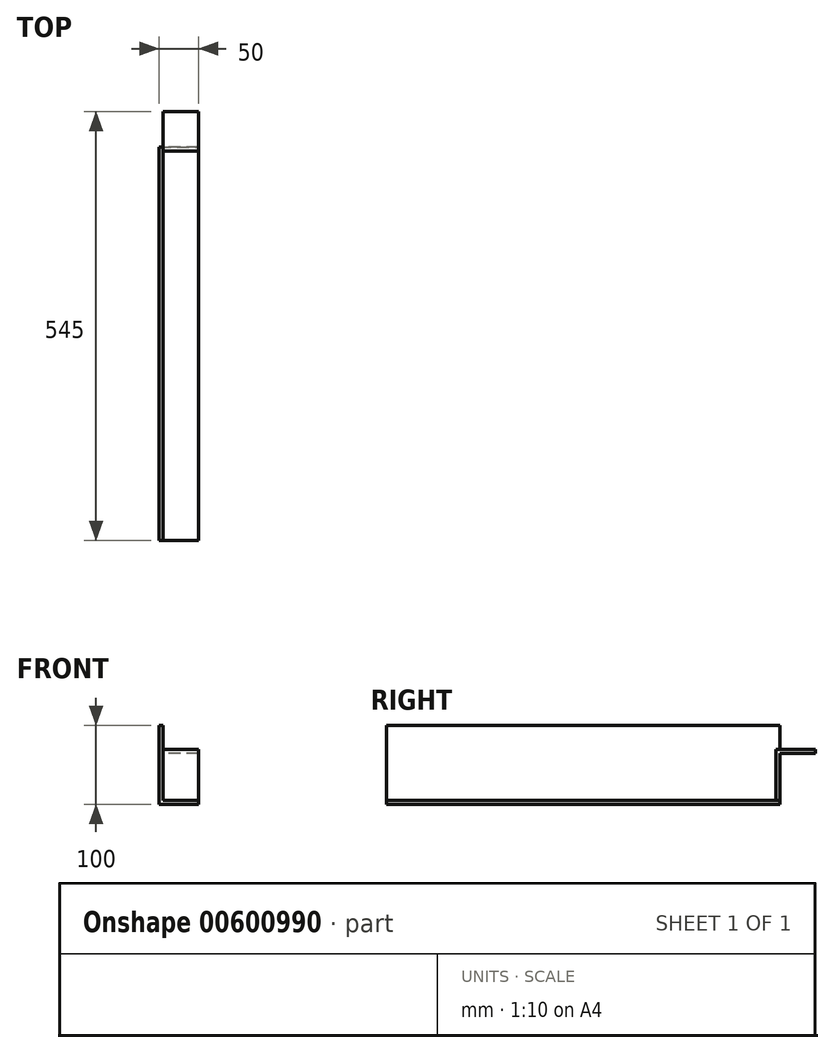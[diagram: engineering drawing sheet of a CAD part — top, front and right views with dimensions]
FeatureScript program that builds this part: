
annotation { "Feature Type Name" : "Feature", "Feature Type Description" : "" }
export const myFeature = defineFeature(function(context is Context, id is Id, definition is map)
    precondition{}
    {
        {
            var Q0;
            Q0=qCreatedBy(makeId("Front.planeOp"),FACE);
            var sketch = newSketch(context, id + "F0", { "sketchPlane" : qUnion([Q0])});
            skLineSegment(sketch, "E0.bottom", {"start": v(0, 0) * mm, "end": v(50, 0) * mm});
            skLineSegment(sketch, "E0.top", {"start": v(0, 100) * mm, "end": v(5, 100) * mm});
            skLineSegment(sketch, "E0.left", {"start": v(0, 0) * mm, "end": v(0, 100) * mm});
            skLineSegment(sketch, "E0.right", {"start": v(50, 0) * mm, "end": v(50, 5) * mm});
            skLineSegment(sketch, "E1.0", {"start": v(5, 5) * mm, "end": v(5, 100) * mm});
            skLineSegment(sketch, "E2.0", {"start": v(5, 5) * mm, "end": v(50, 5) * mm});
            skSolve(sketch);
        }
        {
            var Q0;
            Q0=makeQuery(id+"F0.imprint","IMPRINT",FACE,{"disambiguationData":[TD([[makeQuery(id+"F0.imprint","IMPRINT",EDGE,{"derivedFrom":sQuery(id+"F0.wireOp",EDGE,"E0.bottom")}),1.0]])]});
            extrude(context, id + "F1", {"entities" : qUnion([Q0]), "depth" : 500 * mm, "offsetDistance" : 25 * mm});
        }
        {
            var Q0;
            Q0=qCreatedBy(makeId("Right.planeOp"),FACE);
            var sketch = newSketch(context, id + "F2", { "sketchPlane" : qUnion([Q0])});
            skLineSegment(sketch, "E3.right", {"start": v(-5, 5) * mm, "end": v(-5, 70) * mm});
            skLineSegment(sketch, "E4.MirrorCS", {"start": v(0, 5) * mm, "end": v(-5, 5) * mm});
            skLineSegment(sketch, "E5.MirrorCS", {"start": v(45, 65) * mm, "end": v(45, 70) * mm});
            skLineSegment(sketch, "E6.MirrorCS", {"start": v(0, 5) * mm, "end": v(0, 65) * mm});
            skLineSegment(sketch, "E7.MirrorCS", {"start": v(45, 70) * mm, "end": v(-5, 70) * mm});
            skLineSegment(sketch, "E8.MirrorCS", {"start": v(45, 65) * mm, "end": v(0, 65) * mm});
            skSolve(sketch);
        }
        {
            var Q0;
            Q0=makeQuery(id+"F2.imprint","IMPRINT",FACE,{"disambiguationData":[TD([[makeQuery(id+"F2.imprint","IMPRINT",EDGE,{"derivedFrom":sQuery(id+"F2.wireOp",EDGE,"E3.right")}),-1.0]])]});
            var Q1;
            Q1=makeQuery(id+"F1.opExtrude","SWEPT_FACE",FACE,{"disambiguationData":[OSD([sQuery(id+"F0.wireOp",EDGE,"E1.0")])]});
            extrude(context, id + "F3", {"entities" : qUnion([Q0]), "depth" : 45 * mm, "endBoundEntityFace" : qUnion([Q1]), "offsetDistance" : 25 * mm});
        }
        {
            var Q0;
            Q0=makeQuery(id+"F3.opExtrude","SWEPT_BODY",BODY,{"disambiguationData":[OSD([sQuery(id+"F2.wireOp",EDGE,"E3.right"),sQuery(id+"F2.wireOp",EDGE,"E4.MirrorCS"),sQuery(id+"F2.wireOp",EDGE,"E5.MirrorCS"),sQuery(id+"F2.wireOp",EDGE,"E6.MirrorCS"),sQuery(id+"F2.wireOp",EDGE,"E7.MirrorCS"),sQuery(id+"F2.wireOp",EDGE,"E8.MirrorCS")])]});
            var Q1;
            Q1=makeQuery(id+"F3.opExtrude","CAP_VERTEX",VERTEX,{"disambiguationData":[OSD([sQuery(id+"F2.wireOp",EDGE,"E4.MirrorCS"),sQuery(id+"F2.wireOp",EDGE,"E6.MirrorCS")])],"isStart":false});
            var Q2;
            Q2=makeQuery(id+"F1.opExtrude","CAP_VERTEX",VERTEX,{"disambiguationData":[OSD([sQuery(id+"F0.wireOp",EDGE,"E0.right"),sQuery(id+"F0.wireOp",EDGE,"E2.0")])],"isStart":true});
            transform(context, id + "F4", {"entities" : qUnion([Q0]), "transformType" : TransformType.TRANSLATION_ENTITY, "oppositeDirectionEntity" : false, "transformLine" : qUnion([Q1, Q2]), "makeCopy" : false});
        }
    });
